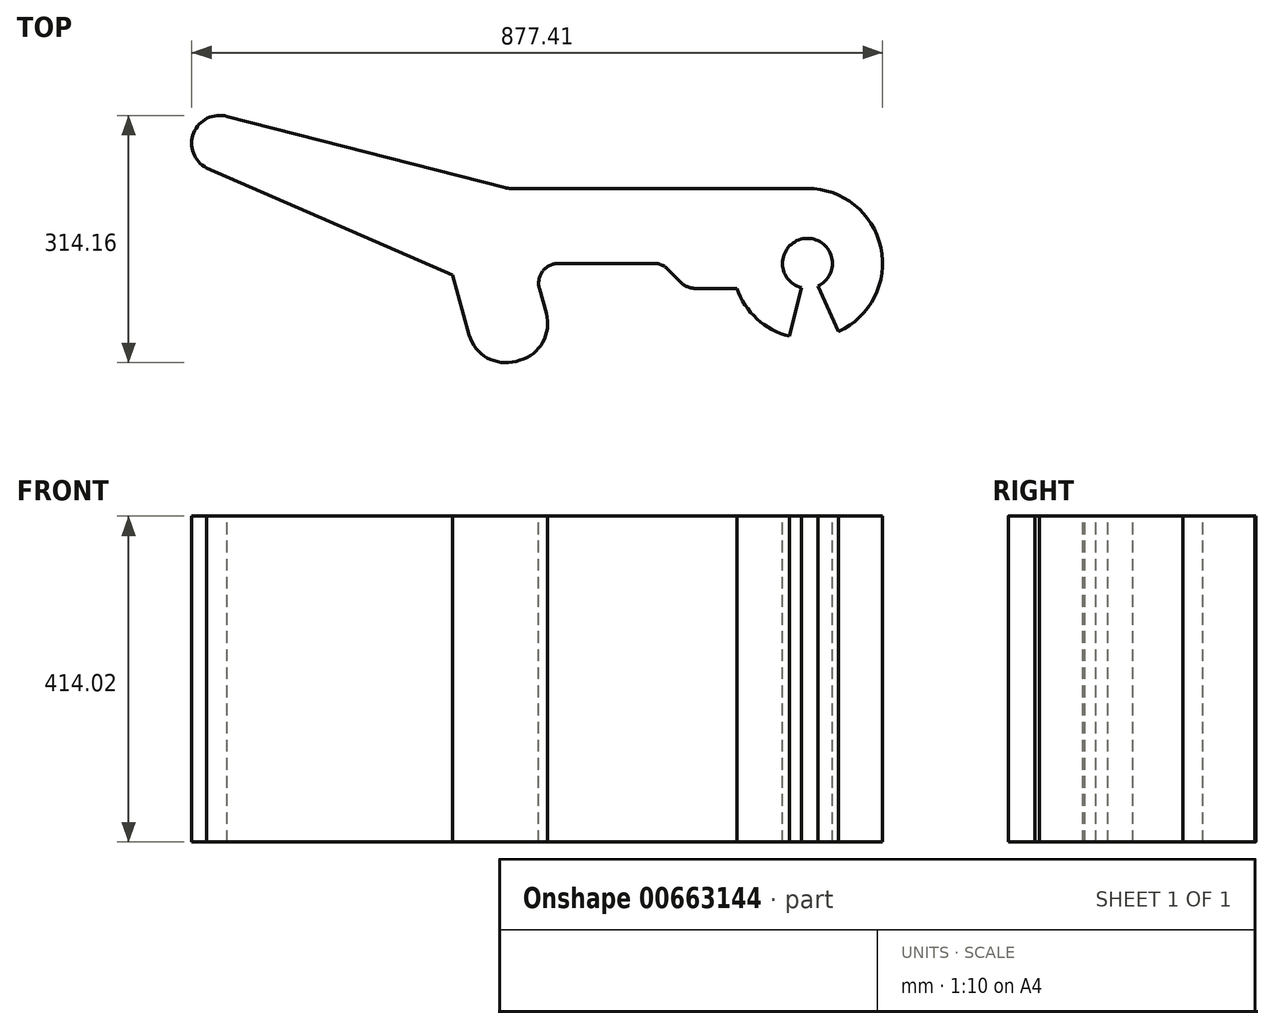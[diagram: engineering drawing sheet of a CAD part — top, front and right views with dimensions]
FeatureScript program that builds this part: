
annotation { "Feature Type Name" : "Feature", "Feature Type Description" : "" }
export const myFeature = defineFeature(function(context is Context, id is Id, definition is map)
    precondition{}
    {
        {
            var Q0;
            Q0=qCreatedBy(makeId("Top.planeOp"),FACE);
            var sketch = newSketch(context, id + "F0", { "sketchPlane" : qUnion([Q0])});
            skArc(sketch, "E0", {"start": v(13.12, -28.91) * mm, "mid": v(5.83, 31.2) * mm, "end": v(-22.68, -22.22) * mm});
            skArc(sketch, "E1", {"start": v(39.36, -86.74) * mm, "mid": v(93.1, 20.13) * mm, "end": v(0, 95.25) * mm});
            skLineSegment(sketch, "E2", {"start": v(0, 95.25) * mm, "end": v(-377.8, 95.25) * mm});
            skLineSegment(sketch, "E3", {"start": v(13.12, -28.91) * mm, "end": v(39.36, -86.74) * mm});
            skLineSegment(sketch, "E4", {"start": v(-89.8, -31.75) * mm, "end": v(-142.63, -31.75) * mm});
            skLineSegment(sketch, "E5", {"start": v(-160.77, -24.13) * mm, "end": v(-176.94, -7.62) * mm});
            skLineSegment(sketch, "E6", {"start": v(-195.08, 0) * mm, "end": v(-316.06, 0) * mm});
            skArc(sketch, "E7", {"start": v(-737.1, 186.67) * mm, "mid": v(-779.66, 165.5) * mm, "end": v(-763.15, 120.92) * mm});
            skPoint(sketch, "E7.third.point", {"position": v(-780.95, 161.62) * mm});
            skPoint(sketch, "E8.orphan", {"position": v(0, -31.75) * mm});
            skArc(sketch, "E9.trimOffspring", {"start": v(-89.8, -31.75) * mm, "mid": v(-80.83, -50.4) * mm, "end": v(-68.04, -66.66) * mm});
            skLineSegment(sketch, "E10", {"start": v(-340.53, -32.22) * mm, "end": v(-331.78, -63.61) * mm});
            skLineSegment(sketch, "E11", {"start": v(-365.3, -123.06) * mm, "end": v(-370.2, -124.43) * mm});
            skLineSegment(sketch, "E12", {"start": v(-429.64, -90.9) * mm, "end": v(-450.79, -15.05) * mm});
            skLineSegment(sketch, "E13", {"start": v(-384.1, 96.05) * mm, "end": v(-737.1, 186.67) * mm});
            skLineSegment(sketch, "E14", {"start": v(-450.79, -15.05) * mm, "end": v(-763.15, 120.92) * mm});
            skPoint(sketch, "E15.visualSharp", {"position": v(-318.82, -110.1) * mm});
            skArc(sketch, "E15.filletArc", {"start": v(-365.3, -123.06) * mm, "mid": v(-336.23, -100.28) * mm, "end": v(-331.78, -63.61) * mm});
            skPoint(sketch, "E16.visualSharp", {"position": v(-416.68, -137.39) * mm});
            skArc(sketch, "E16.filletArc", {"start": v(-429.64, -90.9) * mm, "mid": v(-406.86, -119.97) * mm, "end": v(-370.2, -124.43) * mm});
            skPoint(sketch, "E17.visualSharp", {"position": v(-349.51, 0) * mm});
            skArc(sketch, "E17.filletArc", {"start": v(-316.06, 0) * mm, "mid": v(-336.3, -10.04) * mm, "end": v(-340.53, -32.22) * mm});
            skPoint(sketch, "E18.visualSharp", {"position": v(-153.3, -31.75) * mm});
            skArc(sketch, "E18.filletArc", {"start": v(-160.77, -24.13) * mm, "mid": v(-152.47, -29.77) * mm, "end": v(-142.63, -31.75) * mm});
            skPoint(sketch, "E19.visualSharp", {"position": v(-184.41, 0) * mm});
            skArc(sketch, "E19.filletArc", {"start": v(-176.94, -7.62) * mm, "mid": v(-185.24, -1.98) * mm, "end": v(-195.08, 0) * mm});
            skPoint(sketch, "E20.visualSharp", {"position": v(-381, 95.25) * mm});
            skArc(sketch, "E20.filletArc", {"start": v(-384.1, 96.05) * mm, "mid": v(-380.97, 95.45) * mm, "end": v(-377.8, 95.25) * mm});
            skArc(sketch, "E21", {"start": v(-68.04, -66.66) * mm, "mid": v(-55, -77.76) * mm, "end": v(-40.2, -86.35) * mm});
            skArc(sketch, "E22", {"start": v(-22.68, -22.22) * mm, "mid": v(-18.33, -25.92) * mm, "end": v(-13.4, -28.78) * mm});
            skLineSegment(sketch, "E23", {"start": v(-7.66, -30.81) * mm, "end": v(-22.97, -92.44) * mm});
            skArc(sketch, "E24", {"start": v(-13.4, -28.78) * mm, "mid": v(-10.58, -29.94) * mm, "end": v(-7.66, -30.81) * mm});
            skArc(sketch, "E25", {"start": v(-40.2, -86.35) * mm, "mid": v(-31.73, -89.8) * mm, "end": v(-22.97, -92.44) * mm});
            skSolve(sketch);
        }
        {
            var Q0;
            Q0=makeQuery(id+"F0.imprint","IMPRINT",FACE,{"disambiguationData":[TD([[makeQuery(id+"F0.imprint","IMPRINT",EDGE,{"derivedFrom":sQuery(id+"F0.wireOp",EDGE,"E0")}),-1.0]])]});
            extrude(context, id + "F1", {"entities" : qUnion([Q0]), "oppositeDirection" : true, "depth" : 414.02 * mm, "offsetDistance" : 25.4 * mm});
        }
    });
